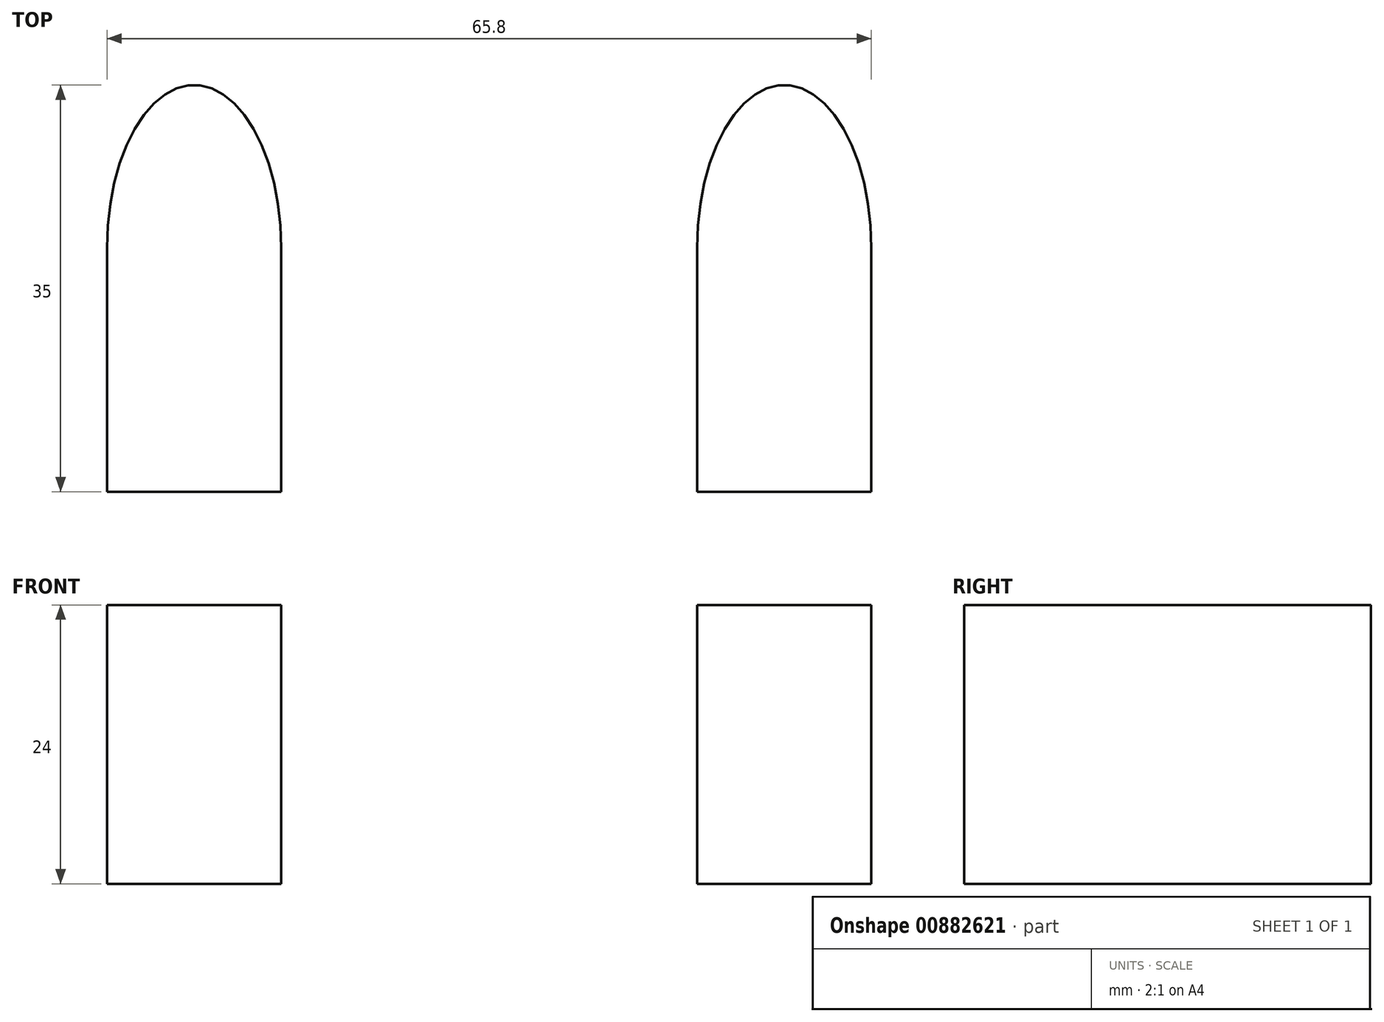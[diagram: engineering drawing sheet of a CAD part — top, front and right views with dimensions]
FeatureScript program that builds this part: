
annotation { "Feature Type Name" : "Feature", "Feature Type Description" : "" }
export const myFeature = defineFeature(function(context is Context, id is Id, definition is map)
    precondition{}
    {
        {
            var Q0;
            Q0=qCreatedBy(makeId("Top.planeOp"),FACE);
            var sketch = newSketch(context, id + "F0", { "sketchPlane" : qUnion([Q0])});
            skLineSegment(sketch, "E0.bottom", {"start": v(7.5, 10.5) * mm, "end": v(-7.5, 10.5) * mm});
            skLineSegment(sketch, "E0.top", {"start": v(7.5, -10.5) * mm, "end": v(-7.5, -10.5) * mm});
            skLineSegment(sketch, "E0.left", {"start": v(7.5, 10.5) * mm, "end": v(7.5, -10.5) * mm});
            skLineSegment(sketch, "E0.right", {"start": v(-7.5, 10.5) * mm, "end": v(-7.5, -10.5) * mm});
            skPoint(sketch, "E0.middle", {"position": v(0, 0) * mm});
            skEllipse(sketch, "E1", {"center": v(0, 10.5) * mm, "majorRadius": 14 * mm, "minorRadius": 7.5 * mm, "majorAxis": v(0, 1)});
            skSolve(sketch);
        }
        {
            var Q0;
            {var subQ0=sQuery(id+"F0.wireOp",EDGE,"E0.bottom");Q0=makeQuery(id+"F0.imprint","IMPRINT",FACE,{"disambiguationData":[TD([[makeQuery(id+"F0.imprint","IMPRINT",EDGE,{"derivedFrom":subQ0}),-1.0]])]});}
            var Q1;
            {var subQ0=sQuery(id+"F0.wireOp",EDGE,"E0.bottom");Q1=makeQuery(id+"F0.imprint","IMPRINT",FACE,{"disambiguationData":[TD([[makeQuery(id+"F0.imprint","IMPRINT",EDGE,{"derivedFrom":subQ0}),1.0]])]});}
            var Q2;
            Q2=makeQuery(id+"F0.imprint","IMPRINT",FACE,{"disambiguationData":[TD([[makeQuery(id+"F0.imprint","IMPRINT",EDGE,{"derivedFrom":sQuery(id+"F0.wireOp",EDGE,"E0.top")}),-1.0]])]});
            extrude(context, id + "F1", {"entities" : qUnion([Q0, Q1, Q2]), "depth" : 24 * mm, "offsetDistance" : 25.4 * mm});
        }
        {
            var Q0;
            Q0=qCreatedBy(makeId("Right.planeOp"),FACE);
            cPlane(context, id + "F2", {"entities" : qUnion([Q0]), "cplaneType" : CPlaneType.OFFSET, "offset" : 25.4 * mm, "width" : 152.4 * mm, "height" : 152.4 * mm});
        }
        {
            var Q0;
            Q0=makeQuery(id+"F1.opExtrude","SWEPT_BODY",BODY,{"disambiguationData":[OSD([sQuery(id+"F0.wireOp",EDGE,"E0.top"),sQuery(id+"F0.wireOp",EDGE,"E0.left"),sQuery(id+"F0.wireOp",EDGE,"E0.right"),sQuery(id+"F0.wireOp",EDGE,"E1")])]});
            var Q1;
            Q1=qCreatedBy(id+"F2.planeOp",FACE);
            mirror(context, id + "F3", {"entities" : qUnion([Q0]), "mirrorPlane" : qUnion([Q1])});
        }
    });
